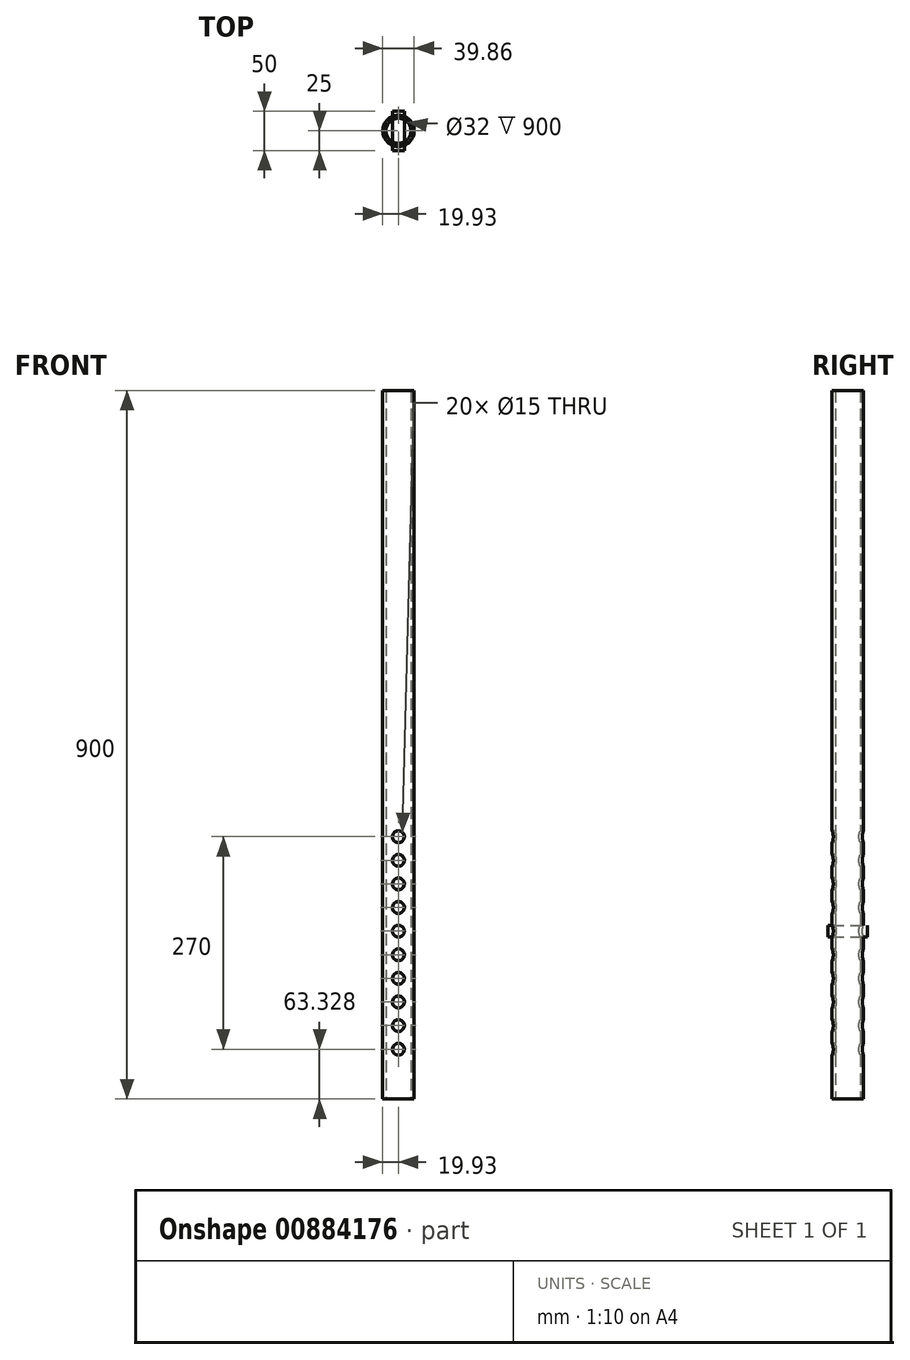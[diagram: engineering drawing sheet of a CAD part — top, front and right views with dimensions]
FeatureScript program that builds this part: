
annotation { "Feature Type Name" : "Feature", "Feature Type Description" : "" }
export const myFeature = defineFeature(function(context is Context, id is Id, definition is map)
    precondition{}
    {
        {
            var Q0;
            Q0=qCreatedBy(makeId("Top.planeOp"),FACE);
            var sketch = newSketch(context, id + "F0", { "sketchPlane" : qUnion([Q0])});
            skCircle(sketch, "E0", {"center": v(0, 0) * mm, "radius": 16 * mm});
            skCircle(sketch, "E1", {"center": v(0, 0) * mm, "radius": 19.93 * mm});
            skSolve(sketch);
        }
        {
            var Q0;
            Q0 = qSketchRegion(id + "F0", true);
            extrude(context, id + "F1", {"entities" : qUnion([Q0]), "depth" : 900 * mm, "offsetDistance" : 25 * mm});
        }
        {
            var Q0;
            Q0=qCreatedBy(makeId("Front.planeOp"),FACE);
            var sketch = newSketch(context, id + "F2", { "sketchPlane" : qUnion([Q0])});
            skCircle(sketch, "E2", {"center": v(0, 63.33) * mm, "radius": 7.5 * mm});
            skCircle(sketch, "E3.1.0.0", {"center": v(0, 93.33) * mm, "radius": 7.5 * mm});
            skCircle(sketch, "E3.2.0.0", {"center": v(0, 123.33) * mm, "radius": 7.5 * mm});
            skLineSegment(sketch, "E3.direction1", {"start": v(0, 63.33) * mm, "end": v(0, 93.33) * mm, "construction": true});
            skCircle(sketch, "E4.0.3.0", {"center": v(0, 153.33) * mm, "radius": 7.5 * mm});
            skCircle(sketch, "E4.0.4.0", {"center": v(0, 183.33) * mm, "radius": 7.5 * mm});
            skCircle(sketch, "E4.0.5.0", {"center": v(0, 213.33) * mm, "radius": 7.5 * mm});
            skCircle(sketch, "E4.0.6.0", {"center": v(0, 243.33) * mm, "radius": 7.5 * mm});
            skCircle(sketch, "E4.0.7.0", {"center": v(0, 273.33) * mm, "radius": 7.5 * mm});
            skCircle(sketch, "E4.0.8.0", {"center": v(0, 303.33) * mm, "radius": 7.5 * mm});
            skCircle(sketch, "E4.0.9.0", {"center": v(0, 333.33) * mm, "radius": 7.5 * mm});
            skSolve(sketch);
        }
        {
            var Q0;
            Q0 = qSketchRegion(id + "F2", true);
            extrude(context, id + "F3", {"entities" : qUnion([Q0]), "operationType" : NewBodyOperationType.REMOVE, "oppositeDirection" : true, "depth" : 60 * mm, "offsetDistance" : 25 * mm, "symmetric" : true});
        }
        {
            var Q0;
            Q0=qCreatedBy(makeId("Front.planeOp"),FACE);
            var sketch = newSketch(context, id + "F4", { "sketchPlane" : qUnion([Q0])});
            skCircle(sketch, "E5", {"center": v(0, 213.38) * mm, "radius": 7.5 * mm});
            skSolve(sketch);
        }
        {
            var Q0;
            Q0 = qSketchRegion(id + "F4", true);
            extrude(context, id + "F5", {"entities" : qUnion([Q0]), "depth" : 50 * mm, "offsetDistance" : 25 * mm, "symmetric" : true});
        }
    });
